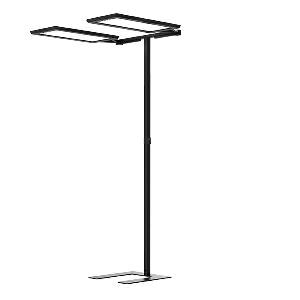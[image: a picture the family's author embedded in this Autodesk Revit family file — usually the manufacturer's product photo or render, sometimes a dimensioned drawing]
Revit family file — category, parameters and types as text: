
# Revit family: yara_doubleu_-_yus_2_15000_vtl_r_sw_cee_s0_c_114268000-00813287_fc99
name_source: partatom
category: Lighting Fixtures
units: mm (PartAtom-declared; Revit-internal decimal feet)

## family parameters
Cut with Voids When Loaded = No
Host = Face
Light Source = No
Part Type = Normal
Room Calculation Point = No
Round Connector Dimension = Use Diameter
Shared = No

## types (1)
- YARA.doubleU - YUS 2/15000/VTL/R/SW/CEE/S0/C (1 x LED, 15000 lm, VTL)
    Apparent Load = 214 VA
    Approval mark = CE
    CIE Flux Codes = 58 87 97 13 100
    Color Rendering = 80-89
    Color Temperature = VTL
    Control Gear = Electronic ballast
    Default Elevation = 1800 mm
    Description = YUS 2/15000/VTL/R/SW/CEE/S0/C|Free-standing luminaire|light source: LED Daylight   |work equipment: Electronic ballast DALI|connected load: 220-240V, 50/60Hz|Power consumption: approx. 210 W|power factor: approx. 0,966|luminous flux: 30000 lm|luminous efficacy: 142 lm/W|light distribution: Direct/indirect|direct ratio: approx. 13 %|color rendering index (CRI): >= 80|chromaticity tolerance:  3 SDCM|technology: Presence and daylight sensor control (PIR)|operation: Wireless switch|luminaire body|material: Aluminium/plastic|surface: Powder coatet|colour: Black|lamp cover: Acrylic (PMMA)|tubular section|material: Steel tube|surface: Powder-coated|Form: Tubular section upright|colour of tubular section: Black|luminaire base|Form: C-form flat|weight (net): approx. 26.0 kg|mains lead: 3.00 m Mains plug CEE 7/VII|Fastening: Floor standing base|glare control: Conical prismatic screen|luminance(L65): <= 2700 cd/m|unified glare rating(4H 8H): <=  16|special features: App control, Asymmetric radiation, Biodynamic light VTL, Direct and indirect lighting component with edge light and light guidetechnology for a homogeneous light exit, Flicker-free, Magnetic control panel, freely positionable, PIR movement and daylight sensor, TALK Bluetooth|Approval mark: VDE - ENEC|
    Frequency = 50 Hz, 60 Hz
    Height = 24 mm  [stored 0.0787402 ft]
    Lamp = 1 x LED
    Lamp Light Flux = 15000 lm
    Lamp count = 1
    Length = 690 mm
    Luminous efficacy = 140 lm/W
    Manufacturer = Waldmann
    ModVariant = No
    Model = 114268000-00813287
    Mounting Place = Floor
    Mounting Type = Freestanding
    Number of Poles = 1
    OnlyDefault = Yes
    Power Factor = 1
    Product Name = YARA.doubleU - YUS 2/15000/VTL/R/SW/CEE/S0/C
    Product group = Free standing luminaire
    ProductGroupID = 13
    Protection Class = Protection class I
    Protection Degree = IP 20
    RLX_Detail_Level = 1
    RlxData = <blob elided: 70289 chars, md5=2e7593a8>
    Socket = socket
    Standby Power = 0 W
    System Light Flux = 30000 lm
    System Power = 214 W
    Type Comments = Product without accessories
    Type Image = yus-r-sw-c.jpg
    URL = http://relux.com
    VarID = ---
    Voltage = 230 V
    Voltage Range = 220-240 V
    Weight = 0.00 kg
    Width = 358 mm

note: [stored X ft] marks values corroborated as IEEE doubles in the binary element streams (Revit-internal decimal feet)

## geometry (parser evidence)
native form markers: Blend x4, Sweep x17
no freeform markers — native parametric forms only
